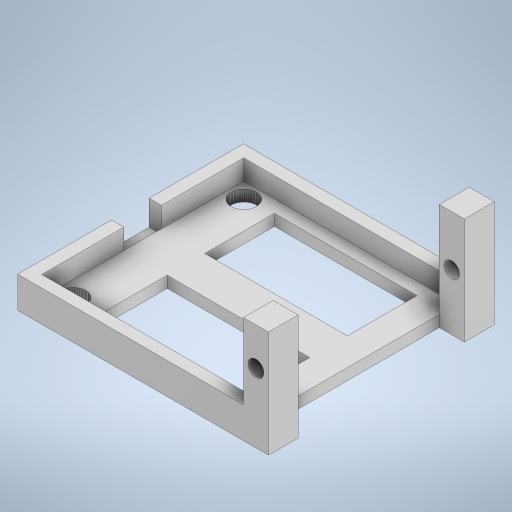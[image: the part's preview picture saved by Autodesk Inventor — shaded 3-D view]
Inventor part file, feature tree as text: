
AUTODESK INVENTOR PART (.ipt)
format: ipt  version: 2024 (Build 280153000, 153)  size: 503,296 bytes
history: native  units: mm
features: other x4, sketch x3, extrude x2, reference x2
ambient origin geometry x8: Origin, YZ Plane, XZ Plane, XY Plane, X Axis, Y Axis, Z Axis, Center Point
bodies: Solid2 (feature_tree), Solid1 (feature_tree)
feature tree (11):
  sketch  "Sketch1"  dims[d0=10.0mm d1=0.0mm d2=1.3mm]
  other  "Work Axis1"
  extrude  "Extrusion1"  Depth=10.0mm
  extrude  "Extrusion2"  [1 undecoded]
  sketch  "Sketch2"  dims[d3=10.0mm d4=0.0mm]
  reference  "Reference1"
  sketch  "Sketch3"
  reference  "Reference2"
  other  "Assembly5"
  other  "NP1_Payload_V2:1"
  other  "Docking_NP1:1"
note: 1 required parameter value undecoded (feature->parameter linkage not recoverable at this tier; creation-order binding heuristic only, values carry confidence <= 0.55)
